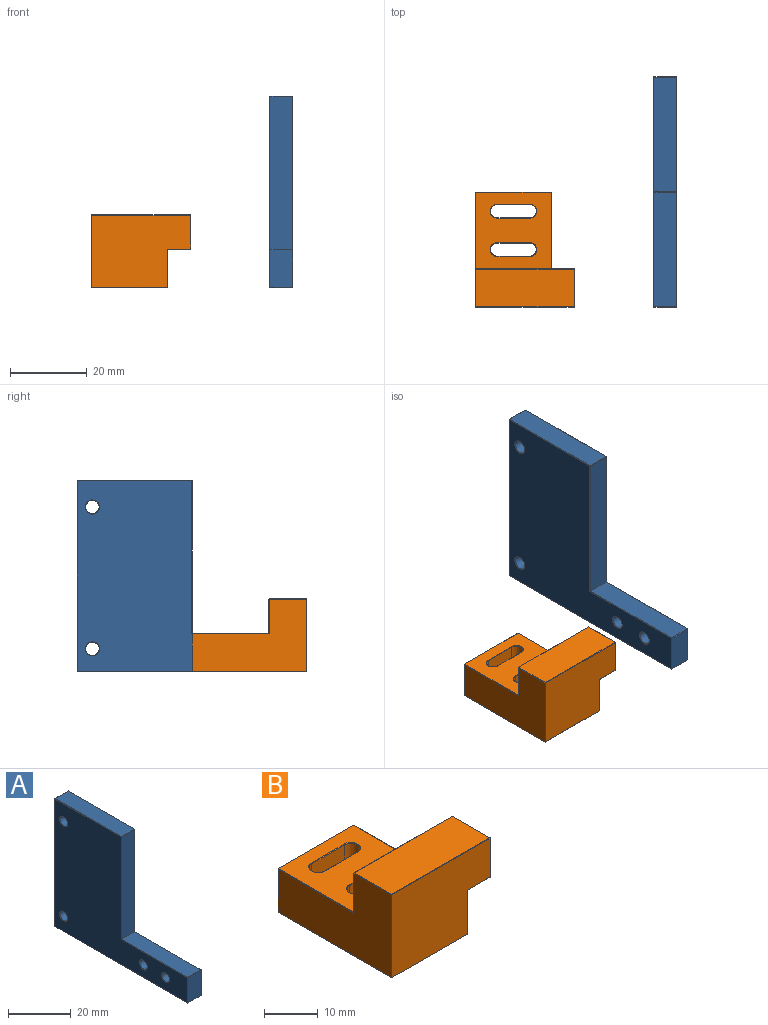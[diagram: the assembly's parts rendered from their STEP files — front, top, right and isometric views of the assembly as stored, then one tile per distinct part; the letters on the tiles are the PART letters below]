
ASSEMBLY  parts=2 mates=1
PART A: 51 faces, bbox 6.1x60x50 mm
  f0: plane 9.8x5.9mm, normal (0,-1,0), area 57.8mm2, adj f31,f36,f39,f42
  f1: plane 59.8x5.9mm, normal (0,0,-1), area 352.8mm2, adj f21,f27,f30,f31
  f2: plane 49.8x5.9mm, normal (0,1,0), area 293.8mm2, adj f16,f17,f20,f21
  f3: plane 29.8x5.9mm, normal (0,0,1), area 175.8mm2, adj f16,f23,f24,f25
  f4: plane 39.9x5.9mm, normal (0,-1,0), area 235.4mm2, adj f5,f24,f33,f34
  f5: plane 29.9x5.9mm, normal (0,0,1), area 176.4mm2, adj f4,f37,f38,f42
  f6: plane 59.8x49.8mm, normal (-1,0,0), area 1736.2mm2, adj f17,f23,f27,f33,f36,f37,f43,f44
  f7: plane 59.8x49.8mm, normal (1,0,0), area 1686mm2, adj f20,f25,f30,f34,f38,f39,f47,f48
  f8: cylinder r=1.75mm len=5.9mm, axis (1,0,0), area 64.9mm2, adj f45,f49
  f9: cylinder r=1.75mm len=5.9mm, axis (1,0,0), area 64.9mm2, adj f46,f50
  f10: cylinder r=1.7mm len=3.4mm, axis (1,0,0), area 32mm2, adj f11,f43
  f11: plane 6.5x6.5mm, normal (1,0,0), area 24.1mm2, adj f10,f12
  f12: cylinder r=3.25mm len=6.5mm, axis (1,0,0), area 59.2mm2, adj f11,f47
  f13: cylinder r=1.7mm len=3.4mm, axis (1,0,0), area 32mm2, adj f14,f44
  f14: plane 6.5x6.5mm, normal (1,0,0), area 24.1mm2, adj f13,f15
  f15: cylinder r=3.25mm len=6.5mm, axis (1,0,0), area 59.2mm2, adj f14,f48
  f16: plane 5.9x0.1mm, normal (0,0.71,0.71), area 0.8mm2, adj f2,f3,f18,f19
  f17: plane 49.8x0.1mm, normal (-0.71,0.71,0), area 7mm2, adj f2,f6,f18,f22
  f18: plane 0.1x0.1mm, normal (-0.58,0.58,0.58), area 0mm2, adj f16,f17,f23
  f19: plane 0.1x0.1mm, normal (0.58,0.58,0.58), area 0mm2, adj f16,f20,f25
  f20: plane 49.8x0.1mm, normal (0.71,0.71,0), area 7mm2, adj f2,f7,f19,f26
  f21: plane 5.9x0.1mm, normal (0,0.71,-0.71), area 0.8mm2, adj f1,f2,f22,f26
  f22: plane 0.1x0.1mm, normal (-0.58,0.58,-0.58), area 0mm2, adj f17,f21,f27
  f23: plane 29.8x0.1mm, normal (-0.71,0,0.71), area 4.2mm2, adj f3,f6,f18,f28
  f24: plane 5.9x0.1mm, normal (0,-0.71,0.71), area 0.8mm2, adj f3,f4,f28,f29
  f25: plane 29.8x0.1mm, normal (0.71,0,0.71), area 4.2mm2, adj f3,f7,f19,f29
  f26: plane 0.1x0.1mm, normal (0.58,0.58,-0.58), area 0mm2, adj f20,f21,f30
  f27: plane 59.8x0.1mm, normal (-0.71,0,-0.71), area 8.5mm2, adj f1,f6,f22,f32
  f28: plane 0.1x0.1mm, normal (-0.58,-0.58,0.58), area 0mm2, adj f23,f24,f33
  f29: plane 0.1x0.1mm, normal (0.58,-0.58,0.58), area 0mm2, adj f24,f25,f34
  f30: plane 59.8x0.1mm, normal (0.71,0,-0.71), area 8.5mm2, adj f1,f7,f26,f35
  f31: plane 5.9x0.1mm, normal (0,-0.71,-0.71), area 0.8mm2, adj f0,f1,f32,f35
  f32: plane 0.1x0.1mm, normal (-0.58,-0.58,-0.58), area 0mm2, adj f27,f31,f36
  f33: plane 40x0.1mm, normal (-0.71,-0.71,0), area 5.6mm2, adj f4,f6,f28,f37
  f34: plane 40x0.1mm, normal (0.71,-0.71,0), area 5.6mm2, adj f4,f7,f29,f38
  f35: plane 0.1x0.1mm, normal (0.58,-0.58,-0.58), area 0mm2, adj f30,f31,f39
  f36: plane 9.8x0.1mm, normal (-0.71,-0.71,0), area 1.4mm2, adj f0,f6,f32,f40
  f37: plane 30x0.1mm, normal (-0.71,0,0.71), area 4.2mm2, adj f5,f6,f33,f40
  f38: plane 30x0.1mm, normal (0.71,0,0.71), area 4.2mm2, adj f5,f7,f34,f41
  f39: plane 9.8x0.1mm, normal (0.71,-0.71,0), area 1.4mm2, adj f0,f7,f35,f41
  f40: plane 0.1x0.1mm, normal (-0.58,-0.58,0.58), area 0mm2, adj f36,f37,f42
  f41: plane 0.1x0.1mm, normal (0.58,-0.58,0.58), area 0mm2, adj f38,f39,f42
  f42: plane 5.9x0.1mm, normal (0,-0.71,0.71), area 0.8mm2, adj f0,f5,f40,f41
  f43: cone r=1.7mm half-angle=45deg, axis (-1,0,0), area 1.6mm2, adj f6,f10
  f44: cone r=1.7mm half-angle=45deg, axis (-1,0,0), area 1.6mm2, adj f6,f13
  f45: cone r=1.75mm half-angle=45deg, axis (-1,0,0), area 1.6mm2, adj f6,f8
  f46: cone r=1.75mm half-angle=45deg, axis (-1,0,0), area 1.6mm2, adj f6,f9
  f47: cone r=3.25mm half-angle=45deg, axis (1,0,0), area 2.9mm2, adj f7,f12
  f48: cone r=3.25mm half-angle=45deg, axis (1,0,0), area 2.9mm2, adj f7,f15
  f49: cone r=1.75mm half-angle=45deg, axis (1,0,0), area 1.6mm2, adj f7,f8
  f50: cone r=1.75mm half-angle=45deg, axis (1,0,0), area 1.6mm2, adj f7,f9
PART B: 81 faces, bbox 26x30x19 mm
  f0: cylinder r=1.7mm len=6.5mm, axis (0,0,1), area 34.7mm2, adj f1,f7,f26,f33
  f1: plane 8.6x6.5mm, normal (0,-1,0), area 55.9mm2, adj f0,f2,f26,f35
  f2: cylinder r=1.7mm len=6.5mm, axis (0,0,1), area 34.7mm2, adj f1,f7,f26,f34
  f3: cylinder r=1.7mm len=6.5mm, axis (0,0,1), area 34.7mm2, adj f4,f6,f31,f37
  f4: plane 8.6x6.5mm, normal (0,-1,0), area 55.9mm2, adj f3,f5,f31,f36
  f5: cylinder r=1.7mm len=6.5mm, axis (0,0,1), area 34.7mm2, adj f4,f6,f31,f38
  f6: plane 8.6x6.5mm, normal (0,1,0), area 55.9mm2, adj f3,f5,f31,f39
  f7: plane 8.6x6.5mm, normal (0,1,0), area 55.9mm2, adj f0,f2,f26,f32
  f8: plane 19.9x19.8mm, normal (0,0,1), area 311.7mm2, adj f15,f32,f33,f34,f35,f36,f37,f38
  f9: plane 29.8x18.8mm, normal (-1,0,0), area 380.2mm2, adj f47,f52,f55,f61,f64,f65
  f10: plane 25.8x18.8mm, normal (0,-1,0), area 425mm2, adj f46,f50,f54,f55,f58,f59
  f11: plane 29.8x9.9mm, normal (1,0,0), area 281.6mm2, adj f14,f15,f41,f43,f44,f50,f71,f72
  f12: plane 19.8x9.8mm, normal (0,1,0), area 194mm2, adj f42,f43,f52,f53
  f13: plane 29.8x19.8mm, normal (0,0,-1), area 404.3mm2, adj f41,f42,f46,f47,f73,f74,f75,f76
  f14: plane 9.9x5.9mm, normal (0,0,-1), area 58.4mm2, adj f11,f15,f54,f62
  f15: plane 25.8x9mm, normal (0,1,0), area 229.6mm2, adj f8,f11,f14,f44,f65,f66,f70
  f16: plane 9.8x8.8mm, normal (1,0,0), area 86.2mm2, adj f58,f62,f66,f67
  f17: plane 25.8x9.8mm, normal (0,0,1), area 252.8mm2, adj f59,f64,f67,f70
  f18: cone r=0mm half-angle=59deg, axis (1,0,0), area 5.7mm2, adj f19
  f19: cylinder r=1.25mm len=9.9mm, axis (1,0,0), area 77.8mm2, adj f18,f72
  f20: cone r=0mm half-angle=59deg, axis (1,0,0), area 5.7mm2, adj f21
  f21: cylinder r=1.25mm len=9.9mm, axis (1,0,0), area 77.8mm2, adj f20,f71
  f22: plane 8.6x3.3mm, normal (0,1,0), area 28.4mm2, adj f23,f25,f26,f73
  f23: cylinder r=3.25mm len=6.5mm, axis (0,0,-1), area 33.7mm2, adj f22,f24,f26,f74
  f24: plane 8.6x3.3mm, normal (0,-1,0), area 28.4mm2, adj f23,f25,f26,f76
  f25: cylinder r=3.25mm len=6.5mm, axis (0,0,-1), area 33.7mm2, adj f22,f24,f26,f75
  f26: plane 15.1x6.5mm, normal (0,0,-1), area 50.8mm2, adj f0,f1,f2,f7,f22,f23,f24,f25
  f27: plane 8.6x3.3mm, normal (0,1,0), area 28.4mm2, adj f28,f30,f31,f77
  f28: cylinder r=3.25mm len=6.5mm, axis (0,0,-1), area 33.7mm2, adj f27,f29,f31,f78
  f29: plane 8.6x3.3mm, normal (0,-1,0), area 28.4mm2, adj f28,f30,f31,f80
  f30: cylinder r=3.25mm len=6.5mm, axis (0,0,-1), area 33.7mm2, adj f27,f29,f31,f79
  f31: plane 15.1x6.5mm, normal (0,0,-1), area 50.8mm2, adj f3,f4,f5,f6,f27,f28,f29,f30
  f32: plane 8.6x0.1mm, normal (0,0.71,0.71), area 1.2mm2, adj f7,f8,f33,f34
  f33: cone r=1.8mm half-angle=45deg, axis (0,0,1), area 0.8mm2, adj f0,f8,f32,f35
  f34: cone r=1.8mm half-angle=45deg, axis (0,0,1), area 0.8mm2, adj f2,f8,f32,f35
  f35: plane 8.6x0.1mm, normal (0,-0.71,0.71), area 1.2mm2, adj f1,f8,f33,f34
  f36: plane 8.6x0.1mm, normal (0,-0.71,0.71), area 1.2mm2, adj f4,f8,f37,f38
  f37: cone r=1.8mm half-angle=45deg, axis (0,0,1), area 0.8mm2, adj f3,f8,f36,f39
  f38: cone r=1.8mm half-angle=45deg, axis (0,0,1), area 0.8mm2, adj f5,f8,f36,f39
  f39: plane 8.6x0.1mm, normal (0,0.71,0.71), area 1.2mm2, adj f6,f8,f37,f38
  f40: plane 0.1x0.1mm, normal (0.58,0.58,-0.58), area 0mm2, adj f41,f42,f43
  f41: plane 29.8x0.1mm, normal (0.71,0,-0.71), area 4.2mm2, adj f11,f13,f40,f45
  f42: plane 19.8x0.1mm, normal (0,0.71,-0.71), area 2.8mm2, adj f12,f13,f40,f48
  f43: plane 9.8x0.1mm, normal (0.71,0.71,0), area 1.4mm2, adj f11,f12,f40,f49
  f44: plane 19.9x0.1mm, normal (0.71,0,0.71), area 2.8mm2, adj f8,f11,f15,f49
  f45: plane 0.1x0.1mm, normal (0.58,-0.58,-0.58), area 0mm2, adj f41,f46,f50
  f46: plane 19.8x0.1mm, normal (0,-0.71,-0.71), area 2.8mm2, adj f10,f13,f45,f51
  f47: plane 29.8x0.1mm, normal (-0.71,0,-0.71), area 4.2mm2, adj f9,f13,f48,f51
  f48: plane 0.1x0.1mm, normal (-0.58,0.58,-0.58), area 0mm2, adj f42,f47,f52
  f49: plane 0.1x0.1mm, normal (0.58,0.58,0.58), area 0mm2, adj f43,f44,f53
  f50: plane 10x0.1mm, normal (0.71,-0.71,0), area 1.4mm2, adj f10,f11,f45,f54
  f51: plane 0.1x0.1mm, normal (-0.58,-0.58,-0.58), area 0mm2, adj f46,f47,f55
  f52: plane 9.8x0.1mm, normal (-0.71,0.71,0), area 1.4mm2, adj f9,f12,f48,f56
  f53: plane 19.8x0.1mm, normal (0,0.71,0.71), area 2.8mm2, adj f8,f12,f49,f56
  f54: plane 6x0.1mm, normal (0,-0.71,-0.71), area 0.8mm2, adj f10,f14,f50,f57
  f55: plane 18.8x0.1mm, normal (-0.71,-0.71,0), area 2.7mm2, adj f9,f10,f51,f60
  f56: plane 0.1x0.1mm, normal (-0.58,0.58,0.58), area 0mm2, adj f52,f53,f61
  f57: plane 0.1x0.1mm, normal (0.58,-0.58,-0.58), area 0mm2, adj f54,f58,f62
  f58: plane 8.8x0.1mm, normal (0.71,-0.71,0), area 1.2mm2, adj f10,f16,f57,f63
  f59: plane 25.8x0.1mm, normal (0,-0.71,0.71), area 3.6mm2, adj f10,f17,f60,f63
  f60: plane 0.1x0.1mm, normal (-0.58,-0.58,0.58), area 0mm2, adj f55,f59,f64
  f61: plane 20x0.1mm, normal (-0.71,0,0.71), area 2.8mm2, adj f8,f9,f56,f65
  f62: plane 9.9x0.1mm, normal (0.71,0,-0.71), area 1.4mm2, adj f14,f16,f57,f66
  f63: plane 0.1x0.1mm, normal (0.58,-0.58,0.58), area 0mm2, adj f58,f59,f67
  f64: plane 9.8x0.1mm, normal (-0.71,0,0.71), area 1.4mm2, adj f9,f17,f60,f68
  f65: plane 9x0.1mm, normal (-0.71,0.71,0), area 1.3mm2, adj f9,f15,f61,f68
  f66: plane 8.9x0.1mm, normal (0.71,0.71,0), area 1.3mm2, adj f15,f16,f62,f69
  f67: plane 9.8x0.1mm, normal (0.71,0,0.71), area 1.4mm2, adj f16,f17,f63,f69
  f68: plane 0.1x0.1mm, normal (-0.58,0.58,0.58), area 0mm2, adj f64,f65,f70
  f69: plane 0.1x0.1mm, normal (0.58,0.58,0.58), area 0mm2, adj f66,f67,f70
  f70: plane 25.8x0.1mm, normal (0,0.71,0.71), area 3.6mm2, adj f15,f17,f68,f69
  f71: cone r=1.25mm half-angle=45deg, axis (1,0,0), area 1.2mm2, adj f11,f21
  f72: cone r=1.25mm half-angle=45deg, axis (1,0,0), area 1.2mm2, adj f11,f19
  f73: plane 8.6x0.1mm, normal (0,0.71,-0.71), area 1.2mm2, adj f13,f22,f74,f75
  f74: cone r=3.35mm half-angle=45deg, axis (0,0,-1), area 1.5mm2, adj f13,f23,f73,f76
  f75: cone r=3.35mm half-angle=45deg, axis (0,0,-1), area 1.5mm2, adj f13,f25,f73,f76
  f76: plane 8.6x0.1mm, normal (0,-0.71,-0.71), area 1.2mm2, adj f13,f24,f74,f75
  f77: plane 8.6x0.1mm, normal (0,0.71,-0.71), area 1.2mm2, adj f13,f27,f78,f79
  f78: cone r=3.35mm half-angle=45deg, axis (0,0,-1), area 1.5mm2, adj f13,f28,f77,f80
  f79: cone r=3.35mm half-angle=45deg, axis (0,0,-1), area 1.5mm2, adj f13,f30,f77,f80
  f80: plane 8.6x0.1mm, normal (0,-0.71,-0.71), area 1.2mm2, adj f13,f29,f78,f79
PLACE A t=(55.98,-4.83,2.49)mm
PLACE B t=(3.3,-4.83,12.49)mm fixed
MATE slider A.f10 <-> B.f20  axis (1,0,0) through (49.98,5.17,7.49)mm
